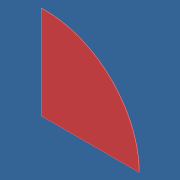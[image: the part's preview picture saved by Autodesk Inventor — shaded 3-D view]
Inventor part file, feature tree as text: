
AUTODESK INVENTOR PART (.ipt)
format: ipt  version: 2012 (Build 160160000, 160)  size: 68,608 bytes
history: native  units: in
note: dims shown in document units (in); Inventor stores cm internally (conversion verified against a paired STEP export)
features: extrude x1, sketch x1
ambient origin geometry x8: Origin, YZ Plane, XZ Plane, XY Plane, X Axis, Y Axis, Z Axis, Center Point
bodies: Solid1 (feature_tree)
feature tree (2):
  extrude  "Extrusion1"  Depth=50.5in
  sketch  "Sketch1"  dims[d0=48.0in d1=50.5in d3=0.125in d4=0.0in d5=2.5in d6=48.0in]
